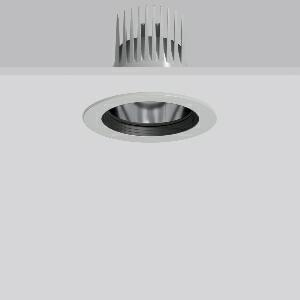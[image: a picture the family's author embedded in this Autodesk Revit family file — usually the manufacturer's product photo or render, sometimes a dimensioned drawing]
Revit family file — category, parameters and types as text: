
# Revit family: heledon_maxi_e_901759_004_3_fc9c
name_source: partatom
category: Lighting Fixtures
units: mm (PartAtom-declared; Revit-internal decimal feet)

## family parameters
Cut with Voids When Loaded = No
Host = Face
Light Source = No
Part Type = Normal
Room Calculation Point = No
Round Connector Dimension = Use Diameter
Shared = No

## types (1)
- HELEDON maxi E (1 x LED Modul 935, 3250 lm, 3500)
    Apparent Load = 25 VA
    Approval mark = CE
    CIE Flux Codes = 97 100 100 100 100
    Color Rendering = 92
    Color Temperature = 3500
    Default Elevation = 1800 mm
    Description = Series: HELEDON maxi
Round recessed downlight. Housing: die-cast aluminium, powder-coated. Black plastic ring and recessed LED to prevent glare from the side. Optical assembly with reflector made of MIRO-Silver with 98% total light reflection for outstanding efficiency - can be changed without tools. Best colour rendering index Ra>90. Suitable for Recessed ceiling mounting. Installation without tools thanks to spring fastening system. Including separate LED converter with connecting cable 600 mm.High quality converter without flickering and stroboscopic effect. Through-wiring box (5 pole) available as accessory. The following accessories can be mounted without use of tools: interchangeable lenses, decorative glasses, honeycomb louvre, clear and frosted diffusers, white interchangeable plastic ring. 
Colour: silver
Diameter: 162 mm
Height: 3 mm
Cut-out diameter: 152 mm
Recess height: 200 mm
Luminaire: recess height: 135 mm
Lamp: LED
Socket: without socket
Colour temperature: 3500K
Colour rendering index (CRI): 92
System power: 25 W
Rated luminous flux: 3250 lm
Luminous efficiency: 130 lm/W
Control gear: Regulated power supply
Protection class: II
Type of protection: IP 20
    Height = 0 mm  [stored 0 ft]
    Lamp = 1 x LED Modul 935
    Lamp Light Flux = 3250 lm
    Lamp count = 1
    Length = 162 mm
    Lifetime = 50000 h
    Luminous efficacy = 130 lm/W
    Manufacturer = RZB
    ModVariant = No
    Model = 901759.004.3
    Mounting Place = Ceiling
    Mounting Type = Recessed
    Number of Poles = 1
    OnlyDefault = Yes
    Power Factor = 1
    Product Name = HELEDON maxi E
    Product group = Recessed downlights
    ProductGroupID = 402
    Protection Class = Protection class II
    Protection Degree = IP 20
    RLX_Detail_Level = 1
    RLX_Emergency_Light_Flux = 0 lm
    RLX_Emergency_Type = 0
    RLX_Emergency_Type_DB = No
    RlxData = <blob elided: 119825 chars, md5=22ee33c6>
    Socket = socket
    Standby Power = 0 W
    System Light Flux = 3250 lm
    System Power = 25 W
    Type Comments = Product without accessories
    Type Image = 901662.004.jpg
    URL = http://relux.com
    VarID = ---
    Voltage = 230 V
    Voltage Range = 220-240 V
    Weight = 0.00 kg
    Width = 0 mm  [stored 0 ft]

note: [stored X ft] marks values corroborated as IEEE doubles in the binary element streams (Revit-internal decimal feet)

## geometry (parser evidence)
native form markers: Blend x4, Sweep x11
no freeform markers — native parametric forms only
